# Revit family: Building-ContenitoriIncasso-GEWISS-24SC-TORRETTE-SCOMPARSA_COPERCHIO
name_source: partatom
category: Apparecchi elettrici
revit_build: Autodesk Revit 2016 (Build: 20161004_0715(x64)
units: mm (PartAtom-declared; Revit-internal decimal feet)

## family parameters
Condiviso = Sì
Host = Superficie
Mantenere orientamento annotazione = Sì
Punto di calcolo locali = Sì
Quota connettore circolare = Usa diametro
Taglio con vuoti quando caricato = No
Tipo di parte = Normale

## types (1)
- Building-ContenitoriIncasso-GEWISS-24SC-TORRETTE-SCOMPARSA_COPERCHIO
    Caratteristiche = Halogen free
    Catalogo = BUILDING
    Catalogo Serie = 24SC
    Codice EAN = 8011564759602
    Codice Electrocod = 200
    Coperchio = Cavo
    Descrizione = TORRETTA A SCOMPARSA 20P COPERCHIO CAVO
    Dim. esterne BxHxP (mm) = 364x98x320
    Glow Wire Test = 850°C
    IDF = 8339f2f8-b1ed-4b1b-a334-5acbcf7e1335
    IDT = 378438b0-1c43-443a-b718-4098a61d4167
    Immagine tipo = GW24602.jpg
    Modello = GW24602
    Modularità interna = 20 moduli SYSTEM
    N. supporti = 4 supporti da 5 moduli System
    Produttore = GEWISS S.p.A.
    Prospetto di default = 1219 mm
    SEO = Torretta
    Scheda Tecnica = https://www.gewiss.com
    TIPO = Torrette a Scomparsa coperchi_GENERICO : GW24602 Torretta a scomparsa 20p con coperchio cavo
    Temperatura di impiego = -5 +45 °C
    URL = https://www.gewiss.com
    Versione file RFA = 19.0

## geometry (parser evidence)
native form markers: Blend x2, Sweep x1
no freeform markers — native parametric forms only
